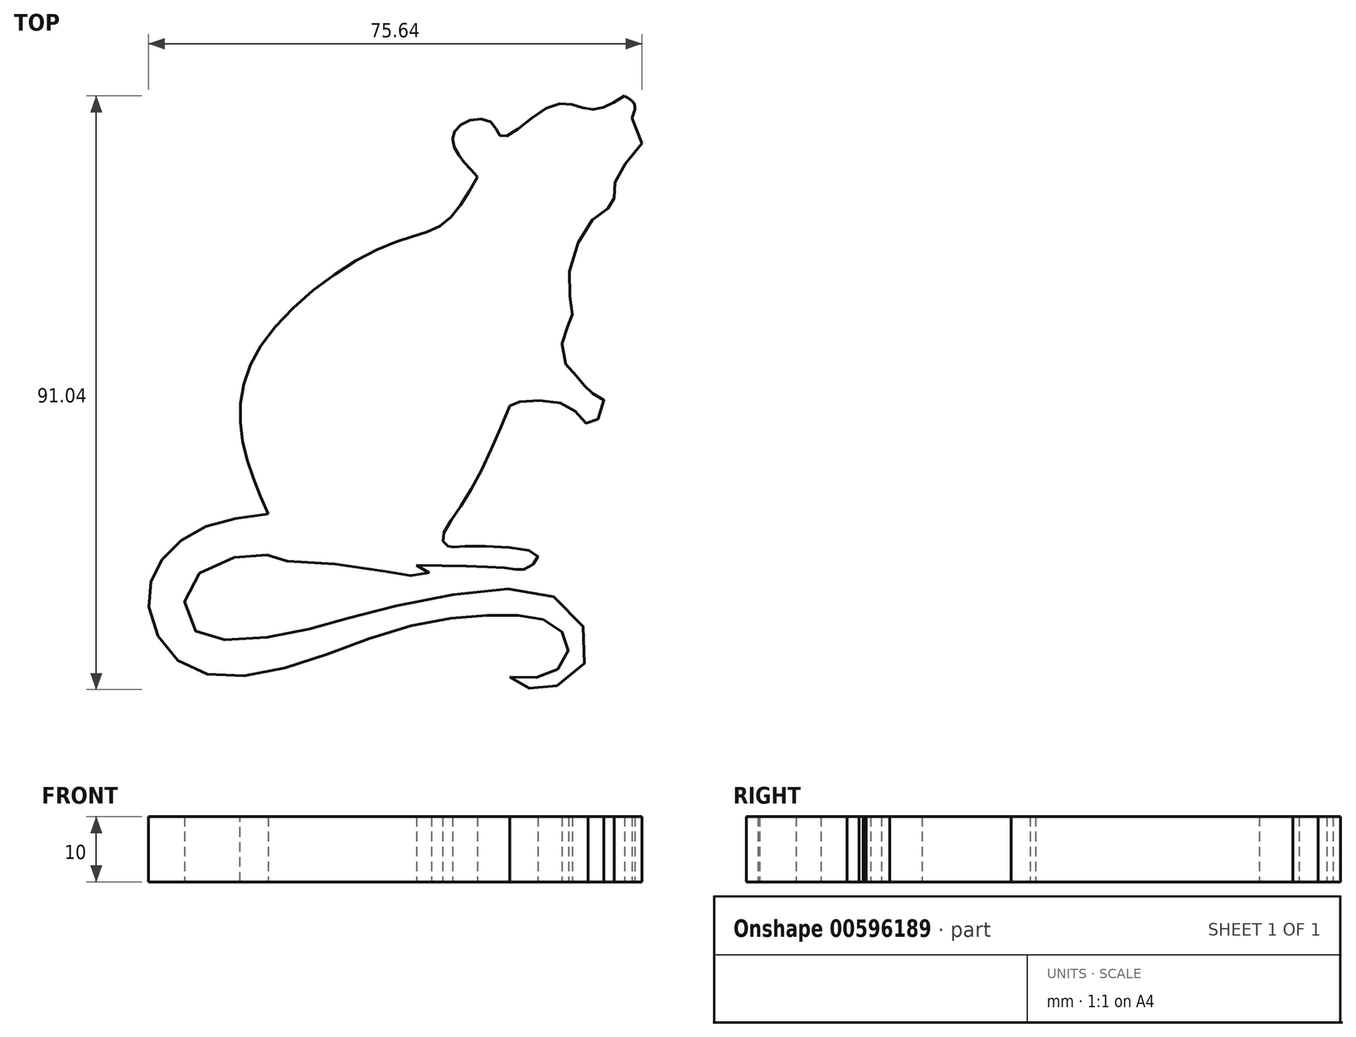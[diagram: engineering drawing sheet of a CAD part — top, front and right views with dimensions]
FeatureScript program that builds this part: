
annotation { "Feature Type Name" : "Feature", "Feature Type Description" : "" }
export const myFeature = defineFeature(function(context is Context, id is Id, definition is map)
    precondition{}
    {
        {
            var Q0;
            Q0=qCreatedBy(makeId("Top.planeOp"),FACE);
            var sketch = newSketch(context, id + "F0", { "sketchPlane" : qUnion([Q0])});
            skFitSpline(sketch, "E0", {"points": [v(-20.33, -12.98) * mm, v(-24.53, 0) * mm, v(-20.71, 13.94) * mm, v(-2.58, 28.06) * mm, v(6.4, 31.5) * mm, v(11.74, 38.75) * mm], "startDerivative": vector(-27.77, 63.87) * mm, "endDerivative": vector(29.02, 52.37) * mm});
            skFitSpline(sketch, "E1", {"points": [v(-20.33, -12.98) * mm, v(-30.83, -15.27) * mm, v(-36.94, -20.43) * mm, v(-38.66, -26.92) * mm, v(-33.89, -35.7) * mm, v(-20.33, -37.23) * mm, v(0, -30.55) * mm, v(15.37, -28.45) * mm, v(22.81, -29.6) * mm, v(25.68, -33.22) * mm, v(23.39, -37.23) * mm, v(16.7, -38) * mm], "startDerivative": vector(-115.27, -14.05) * mm, "endDerivative": vector(-96.25, 5.27) * mm});
            skFitSpline(sketch, "E2", {"points": [v(16.7, -38) * mm, v(19.17, -39.52) * mm, v(23.39, -39.52) * mm, v(28.54, -34.75) * mm, v(24.91, -26.54) * mm, v(11.74, -24.82) * mm, v(-6.4, -28.45) * mm, v(-16.13, -31.12) * mm, v(-27.01, -32.26) * mm, v(-31.98, -30.35) * mm, v(-32.74, -24.44) * mm, v(-27.01, -20.05) * mm, v(-20.33, -19.28) * mm, v(-18.42, -20.05) * mm, v(-4.87, -21.2) * mm, v(1.43, -22.53) * mm, v(2, -21.95) * mm, v(4.68, -21.95) * mm, v(2.39, -20.8) * mm], "startDerivative": vector(60.82, -47.1) * mm, "endDerivative": vector(-108, 44.82) * mm});
            skFitSpline(sketch, "E3", {"points": [v(2.39, -20.8) * mm, v(16.7, -21.33) * mm, v(19.17, -21.33) * mm, v(20.9, -19.28) * mm, v(9.45, -17.95) * mm, v(7.35, -17.95) * mm, v(6.4, -16.8) * mm, v(9.64, -11.07) * mm, v(16.7, 3.63) * mm], "startDerivative": vector(91.17, -1.18) * mm, "endDerivative": vector(32.9, 78.23) * mm});
            skFitSpline(sketch, "E4", {"points": [v(16.7, 3.63) * mm, v(18.04, 4.2) * mm, v(23.77, 4.2) * mm, v(27.2, 2.3) * mm, v(29.3, 0.76) * mm, v(31.02, 4.77) * mm, v(28.73, 5.73) * mm, v(27.78, 7.45) * mm, v(25.68, 9.35) * mm, v(24.91, 14.5) * mm, v(26.25, 17.18) * mm, v(25.68, 22.53) * mm, v(29.5, 32.26) * mm, v(32.55, 34.75) * mm, v(32.74, 37.6) * mm, v(36.94, 43.9) * mm], "startDerivative": vector(25.2, 15.66) * mm, "endDerivative": vector(62.72, 72.38) * mm});
            skFitSpline(sketch, "E5", {"points": [v(36.94, 43.9) * mm, v(35.41, 47.73) * mm], "startDerivative": vector(-1.53, 3.82) * mm, "endDerivative": vector(-1.53, 3.82) * mm});
            skFitSpline(sketch, "E6", {"points": [v(35.41, 47.73) * mm, v(35.8, 49.83) * mm, v(34.27, 51.16) * mm], "startDerivative": vector(1.73, 4.51) * mm, "endDerivative": vector(-4.04, 2.35) * mm});
            skFitSpline(sketch, "E7", {"points": [v(34.27, 51.16) * mm, v(29.12, 49.06) * mm, v(23.58, 49.83) * mm, v(15.56, 44.86) * mm, v(14.03, 46.96) * mm, v(9.83, 47.15) * mm, v(7.92, 44.67) * mm, v(9.07, 41.8) * mm, v(11.74, 38.75) * mm], "startDerivative": vector(-37.42, -23.88) * mm, "endDerivative": vector(24.02, -25.23) * mm});
            skSolve(sketch);
        }
        {
            var Q0;
            Q0 = qSketchRegion(id + "F0", true);
            extrude(context, id + "F1", {"entities" : qUnion([Q0]), "depth" : 10 * mm, "offsetDistance" : 25 * mm});
        }
    });
